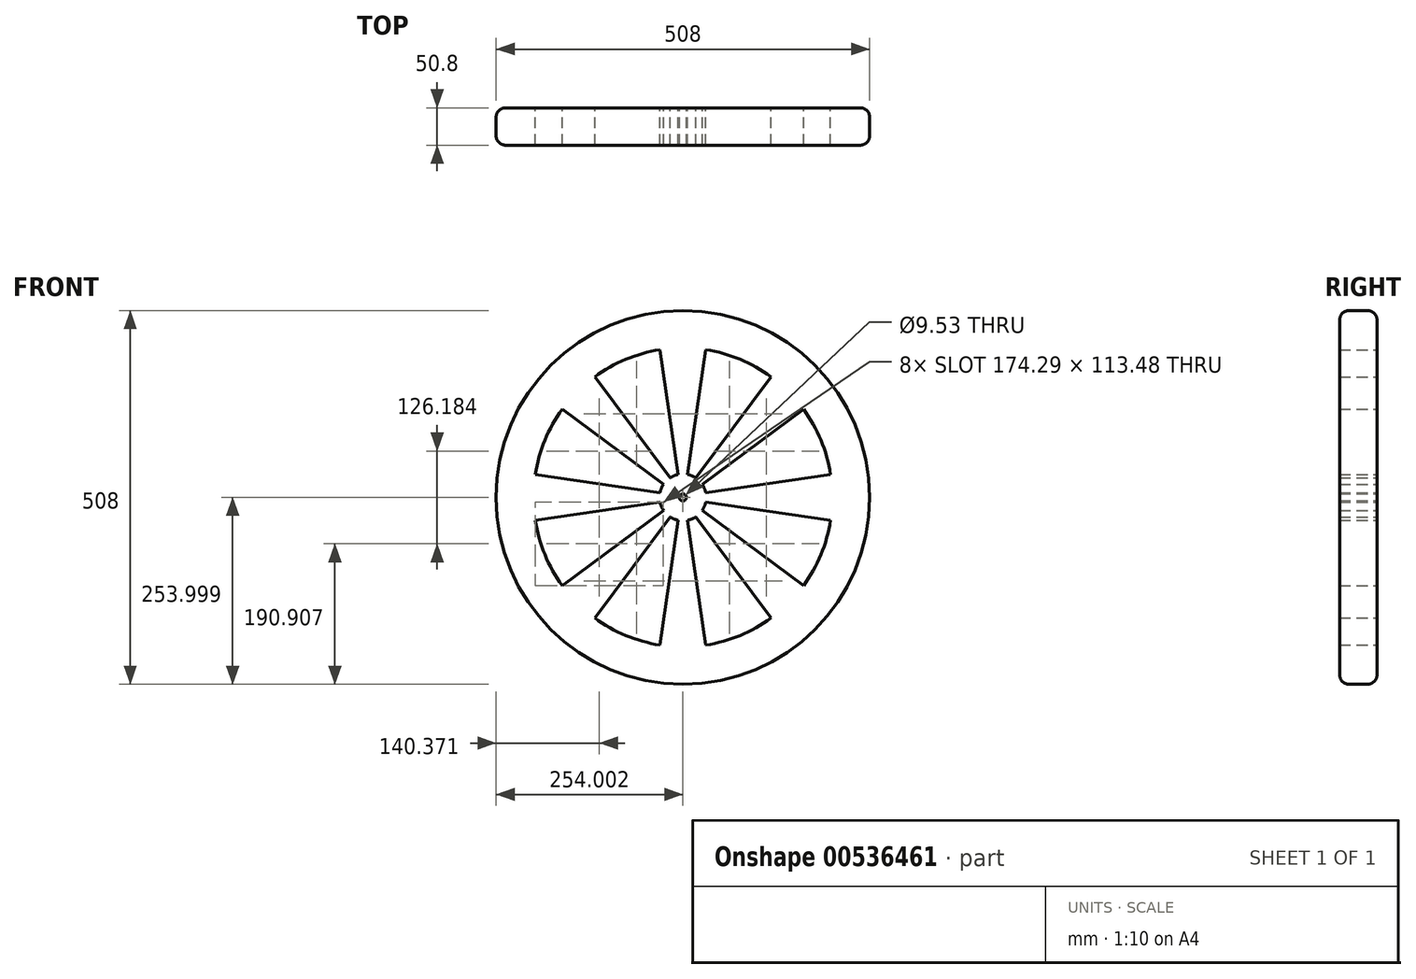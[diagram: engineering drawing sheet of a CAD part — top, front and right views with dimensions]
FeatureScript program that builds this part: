
annotation { "Feature Type Name" : "Feature", "Feature Type Description" : "" }
export const myFeature = defineFeature(function(context is Context, id is Id, definition is map)
    precondition{}
    {
        {
            var Q0;
            Q0=qCreatedBy(makeId("Front.planeOp"),FACE);
            var sketch = newSketch(context, id + "F0", { "sketchPlane" : qUnion([Q0])});
            skCircle(sketch, "E0", {"center": v(-79.28, 3.37) * mm, "radius": 254 * mm});
            skCircle(sketch, "E1", {"center": v(-79.28, 3.37) * mm, "radius": 4.76 * mm});
            skArc(sketch, "E2.0", {"start": v(-280.05, -27.94) * mm, "mid": v(-267.01, -74.4) * mm, "end": v(-243.38, -116.46) * mm});
            skLineSegment(sketch, "E3.0", {"start": v(-72.93, 34.48) * mm, "end": v(-47.97, 204.14) * mm});
            skLineSegment(sketch, "E4.0", {"start": v(-85.63, 34.48) * mm, "end": v(-110.58, 204.14) * mm});
            skLineSegment(sketch, "E5.1.0", {"start": v(-96.78, 29.86) * mm, "end": v(-199.11, 167.47) * mm});
            skLineSegment(sketch, "E5.1.1", {"start": v(-105.76, 20.88) * mm, "end": v(-243.38, 123.2) * mm});
            skLineSegment(sketch, "E5.2.0", {"start": v(-110.39, 9.72) * mm, "end": v(-280.05, 34.67) * mm});
            skLineSegment(sketch, "E5.2.1", {"start": v(-110.39, -2.98) * mm, "end": v(-280.05, -27.94) * mm});
            skLineSegment(sketch, "E5.3.0", {"start": v(-105.76, -14.14) * mm, "end": v(-243.38, -116.46) * mm});
            skLineSegment(sketch, "E5.3.1", {"start": v(-96.78, -23.12) * mm, "end": v(-199.11, -160.74) * mm});
            skLineSegment(sketch, "E5.4.0", {"start": v(-85.63, -27.74) * mm, "end": v(-110.58, -197.4) * mm});
            skLineSegment(sketch, "E5.4.1", {"start": v(-72.93, -27.74) * mm, "end": v(-47.97, -197.4) * mm});
            skLineSegment(sketch, "E5.5.0", {"start": v(-61.77, -23.12) * mm, "end": v(40.56, -160.74) * mm});
            skLineSegment(sketch, "E5.5.1", {"start": v(-52.8, -14.14) * mm, "end": v(84.83, -116.46) * mm});
            skLineSegment(sketch, "E5.6.0", {"start": v(-48.17, -2.98) * mm, "end": v(121.5, -27.94) * mm});
            skLineSegment(sketch, "E5.6.1", {"start": v(-48.17, 9.72) * mm, "end": v(121.5, 34.67) * mm});
            skLineSegment(sketch, "E5.7.0", {"start": v(-52.8, 20.88) * mm, "end": v(84.83, 123.2) * mm});
            skLineSegment(sketch, "E5.7.1", {"start": v(-61.77, 29.86) * mm, "end": v(40.56, 167.47) * mm});
            skPoint(sketch, "E6.orphan", {"position": v(-83.88, 2.14) * mm});
            skPoint(sketch, "E7.orphan", {"position": v(-83.4, 0.99) * mm});
            skPoint(sketch, "E8.orphan", {"position": v(-81.66, -0.76) * mm});
            skPoint(sketch, "E9.orphan", {"position": v(-80.51, -1.23) * mm});
            skPoint(sketch, "E10.orphan", {"position": v(-78.05, -1.23) * mm});
            skPoint(sketch, "E11.orphan", {"position": v(-76.9, -0.76) * mm});
            skPoint(sketch, "E12.orphan", {"position": v(-74.68, 2.14) * mm});
            skPoint(sketch, "E13.orphan", {"position": v(-75.15, 0.99) * mm});
            skPoint(sketch, "E14.orphan", {"position": v(-78.05, 7.97) * mm});
            skPoint(sketch, "E15.orphan", {"position": v(-76.9, 7.5) * mm});
            skPoint(sketch, "E16.orphan", {"position": v(-75.15, 5.75) * mm});
            skPoint(sketch, "E17.orphan", {"position": v(-74.68, 4.6) * mm});
            skPoint(sketch, "E18.orphan", {"position": v(-81.66, 7.5) * mm});
            skPoint(sketch, "E19.orphan", {"position": v(-80.51, 7.97) * mm});
            skPoint(sketch, "E20.orphan", {"position": v(-83.88, 4.6) * mm});
            skPoint(sketch, "E21.orphan", {"position": v(-83.4, 5.75) * mm});
            skArc(sketch, "E22.trimOffspring", {"start": v(-243.38, 123.2) * mm, "mid": v(-267.01, 81.13) * mm, "end": v(-280.05, 34.67) * mm});
            skArc(sketch, "E23.trimOffspring", {"start": v(-110.58, 204.14) * mm, "mid": v(-157.04, 191.1) * mm, "end": v(-199.11, 167.47) * mm});
            skArc(sketch, "E24.trimOffspring", {"start": v(40.56, 167.47) * mm, "mid": v(-1.52, 191.1) * mm, "end": v(-47.97, 204.14) * mm});
            skArc(sketch, "E25.trimOffspring", {"start": v(121.5, 34.67) * mm, "mid": v(108.45, 81.13) * mm, "end": v(84.83, 123.2) * mm});
            skArc(sketch, "E26.trimOffspring", {"start": v(-199.11, -160.74) * mm, "mid": v(-157.04, -184.36) * mm, "end": v(-110.58, -197.4) * mm});
            skArc(sketch, "E27.trimOffspring", {"start": v(-47.97, -197.4) * mm, "mid": v(-1.52, -184.36) * mm, "end": v(40.56, -160.74) * mm});
            skArc(sketch, "E28.trimOffspring", {"start": v(84.83, -116.46) * mm, "mid": v(108.45, -74.4) * mm, "end": v(121.5, -27.94) * mm});
            skArc(sketch, "E29", {"start": v(-61.77, 29.86) * mm, "mid": v(-67.13, 32.7) * mm, "end": v(-72.93, 34.48) * mm});
            skArc(sketch, "E30.trimOffspring", {"start": v(-85.63, 34.48) * mm, "mid": v(-91.43, 32.7) * mm, "end": v(-96.78, 29.86) * mm});
            skArc(sketch, "E31.trimOffspring", {"start": v(-105.76, 20.88) * mm, "mid": v(-108.61, 15.52) * mm, "end": v(-110.39, 9.72) * mm});
            skArc(sketch, "E32.trimOffspring", {"start": v(-110.39, -2.98) * mm, "mid": v(-108.61, -8.78) * mm, "end": v(-105.76, -14.14) * mm});
            skArc(sketch, "E33.trimOffspring", {"start": v(-96.78, -23.12) * mm, "mid": v(-91.43, -25.96) * mm, "end": v(-85.63, -27.74) * mm});
            skArc(sketch, "E34.trimOffspring", {"start": v(-72.93, -27.74) * mm, "mid": v(-67.13, -25.96) * mm, "end": v(-61.77, -23.12) * mm});
            skArc(sketch, "E35.trimOffspring", {"start": v(-52.8, -14.14) * mm, "mid": v(-49.94, -8.78) * mm, "end": v(-48.17, -2.98) * mm});
            skArc(sketch, "E36.trimOffspring", {"start": v(-48.17, 9.72) * mm, "mid": v(-49.94, 15.52) * mm, "end": v(-52.8, 20.88) * mm});
            skLineSegment(sketch, "E37.trimOffspring", {"start": v(-229.42, 208.24) * mm, "end": v(-229.52, 208.36) * mm});
            skLineSegment(sketch, "E38.trimOffspring", {"start": v(-284.15, 153.52) * mm, "end": v(-284.27, 153.6) * mm});
            skLineSegment(sketch, "E39.trimOffspring", {"start": v(-117.97, 254.4) * mm, "end": v(-118, 254.55) * mm});
            skLineSegment(sketch, "E40.trimOffspring", {"start": v(-40.58, 254.4) * mm, "end": v(-40.56, 254.55) * mm});
            skLineSegment(sketch, "E41.trimOffspring", {"start": v(125.6, 153.52) * mm, "end": v(125.72, 153.6) * mm});
            skLineSegment(sketch, "E42.trimOffspring", {"start": v(70.87, 208.24) * mm, "end": v(70.96, 208.36) * mm});
            skLineSegment(sketch, "E43.trimOffspring", {"start": v(171.76, 42.07) * mm, "end": v(171.9, 42.09) * mm});
            skLineSegment(sketch, "E44.trimOffspring", {"start": v(171.76, -35.33) * mm, "end": v(171.9, -35.35) * mm});
            skLineSegment(sketch, "E45.trimOffspring", {"start": v(125.6, -146.78) * mm, "end": v(125.72, -146.87) * mm});
            skLineSegment(sketch, "E46.trimOffspring", {"start": v(70.87, -201.5) * mm, "end": v(70.96, -201.62) * mm});
            skLineSegment(sketch, "E47.trimOffspring", {"start": v(-40.58, -247.67) * mm, "end": v(-40.56, -247.82) * mm});
            skLineSegment(sketch, "E48.trimOffspring", {"start": v(-117.97, -247.67) * mm, "end": v(-118, -247.82) * mm});
            skLineSegment(sketch, "E49.trimOffspring", {"start": v(-229.42, -201.5) * mm, "end": v(-229.52, -201.62) * mm});
            skLineSegment(sketch, "E50.trimOffspring", {"start": v(-284.15, -146.78) * mm, "end": v(-284.27, -146.87) * mm});
            skLineSegment(sketch, "E51.trimOffspring", {"start": v(-330.31, -35.33) * mm, "end": v(-330.46, -35.35) * mm});
            skLineSegment(sketch, "E52.trimOffspring", {"start": v(-330.31, 42.07) * mm, "end": v(-330.46, 42.09) * mm});
            skSolve(sketch);
        }
        {
            var Q0;
            Q0 = qSketchRegion(id + "F0", true);
            extrude(context, id + "F1", {"entities" : qUnion([Q0]), "depth" : 50.8 * mm, "offsetDistance" : 25.4 * mm});
        }
        {
            var Q0;
            Q0=makeQuery(id+"F1.opExtrude","CAP_EDGE",EDGE,{"disambiguationData":[OSD([sQuery(id+"F0.wireOp",EDGE,"E0")])],"isStart":false});
            var Q1;
            Q1=makeQuery(id+"F1.opExtrude","CAP_EDGE",EDGE,{"disambiguationData":[OSD([sQuery(id+"F0.wireOp",EDGE,"E0")])],"isStart":true});
            fillet(context, id + "F2", {"entities" : qUnion([Q0, Q1]), "radius" : 12.7 * mm, "tangentPropagation" : true, "allowEdgeOverflow" : false});
        }
    });
